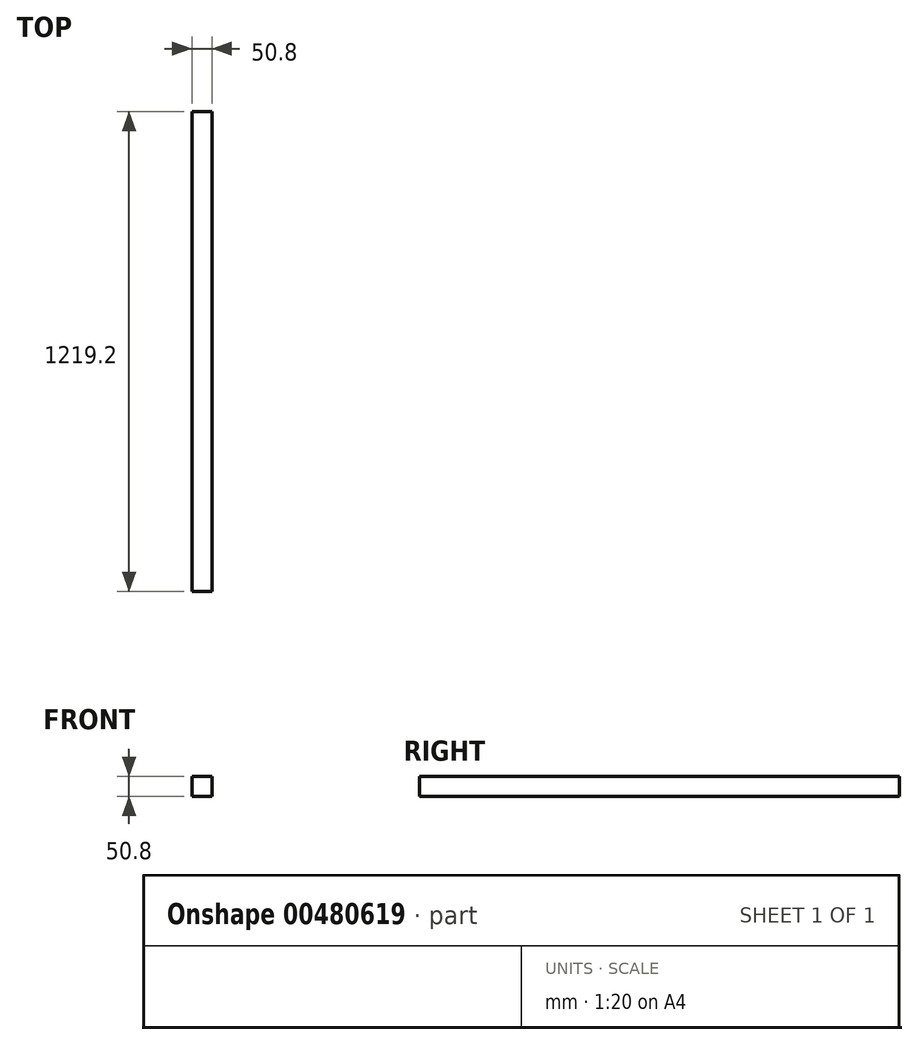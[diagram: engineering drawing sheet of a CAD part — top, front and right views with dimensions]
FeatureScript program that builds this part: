
annotation { "Feature Type Name" : "Feature", "Feature Type Description" : "" }
export const myFeature = defineFeature(function(context is Context, id is Id, definition is map)
    precondition{}
    {
        {
            var Q0;
            Q0=qCreatedBy(makeId("Front.planeOp"),FACE);
            var sketch = newSketch(context, id + "F0", { "sketchPlane" : qUnion([Q0])});
            skLineSegment(sketch, "E0.bottom", {"start": v(25.4, 25.4) * mm, "end": v(-25.4, 25.4) * mm});
            skLineSegment(sketch, "E0.top", {"start": v(25.4, -25.4) * mm, "end": v(-25.4, -25.4) * mm});
            skLineSegment(sketch, "E0.left", {"start": v(25.4, 25.4) * mm, "end": v(25.4, -25.4) * mm});
            skLineSegment(sketch, "E0.right", {"start": v(-25.4, 25.4) * mm, "end": v(-25.4, -25.4) * mm});
            skPoint(sketch, "E0.middle", {"position": v(0, 0) * mm});
            skSolve(sketch);
        }
        {
            var Q0;
            Q0 = qSketchRegion(id + "F0", true);
            extrude(context, id + "F1", {"entities" : qUnion([Q0]), "depth" : 1219.2 * mm});
        }
    });
